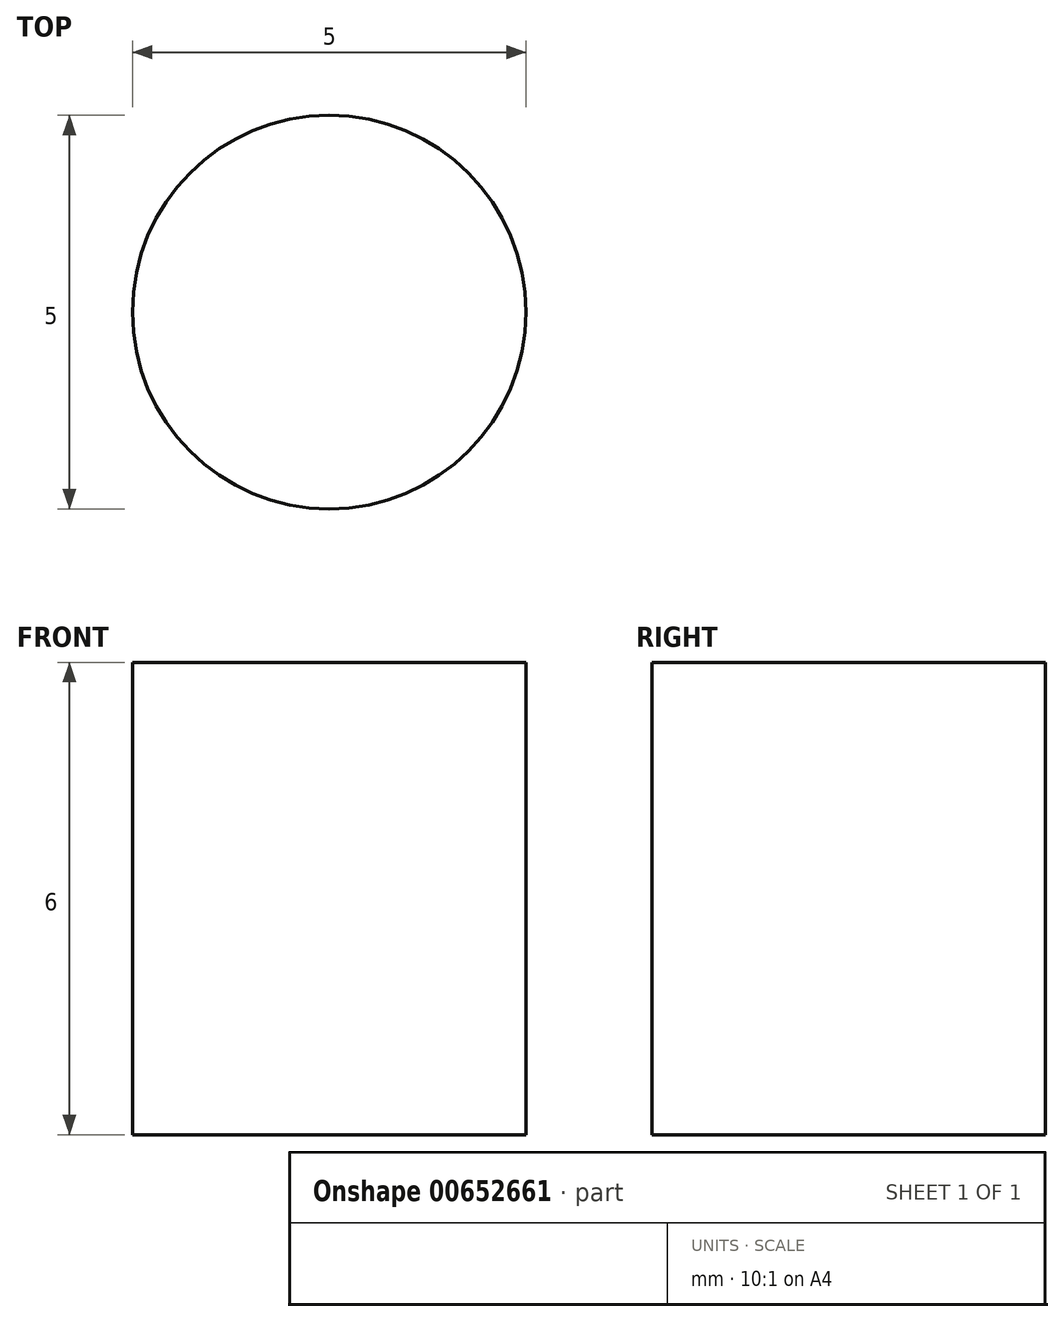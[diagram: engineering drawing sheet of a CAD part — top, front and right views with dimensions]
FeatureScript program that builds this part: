
annotation { "Feature Type Name" : "Feature", "Feature Type Description" : "" }
export const myFeature = defineFeature(function(context is Context, id is Id, definition is map)
    precondition{}
    {
        {
            var Q0;
            Q0=qCreatedBy(makeId("Top.planeOp"),FACE);
            var sketch = newSketch(context, id + "F0", { "sketchPlane" : qUnion([Q0])});
            skCircle(sketch, "E0", {"center": v(0, 0) * mm, "radius": 2.5 * mm});
            skSolve(sketch);
        }
        {
            var Q0;
            Q0 = qSketchRegion(id + "F0", true);
            extrude(context, id + "F1", {"entities" : qUnion([Q0]), "depth" : 6 * mm, "offsetDistance" : 25 * mm});
        }
    });
